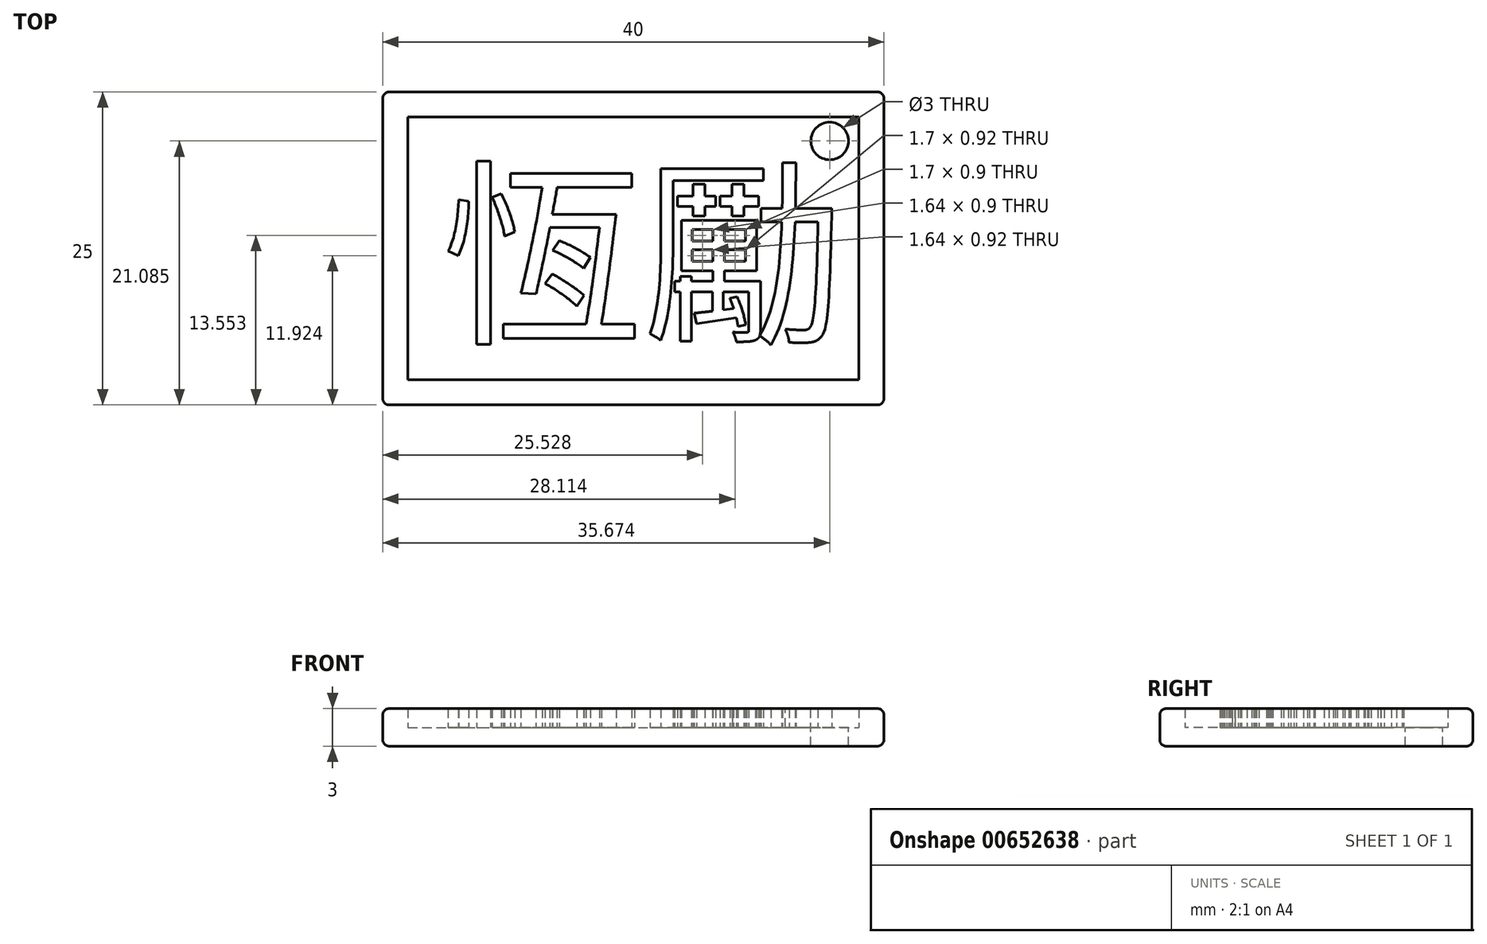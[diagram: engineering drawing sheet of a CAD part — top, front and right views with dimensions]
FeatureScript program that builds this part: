
annotation { "Feature Type Name" : "Feature", "Feature Type Description" : "" }
export const myFeature = defineFeature(function(context is Context, id is Id, definition is map)
    precondition{}
    {
        {
            var Q0;
            Q0=qCreatedBy(makeId("Top.planeOp"),FACE);
            var sketch = newSketch(context, id + "F0", { "sketchPlane" : qUnion([Q0])});
            skLineSegment(sketch, "E0.bottom", {"start": v(-20, -10.33) * mm, "end": v(20, -10.33) * mm});
            skLineSegment(sketch, "E0.top", {"start": v(20, 14.67) * mm, "end": v(-20, 14.67) * mm});
            skLineSegment(sketch, "E0.left", {"start": v(-20, -10.33) * mm, "end": v(-20, 14.67) * mm});
            skLineSegment(sketch, "E0.right", {"start": v(20, 14.67) * mm, "end": v(20, -10.33) * mm});
            skPoint(sketch, "E0.middle", {"position": v(0, 14.67) * mm});
            skSolve(sketch);
        }
        {
            var Q0;
            Q0 = qSketchRegion(id + "F0", true);
            extrude(context, id + "F1", {"entities" : qUnion([Q0]), "depth" : 1.5 * mm, "offsetDistance" : 25 * mm});
        }
        {
            var Q0;
            Q0=makeQuery(id+"F1.opExtrude","CAP_FACE",FACE,{"disambiguationData":[OSD([sQuery(id+"F0.wireOp",EDGE,"E0.bottom"),sQuery(id+"F0.wireOp",EDGE,"E0.top"),sQuery(id+"F0.wireOp",EDGE,"E0.left"),sQuery(id+"F0.wireOp",EDGE,"E0.right")])],"isStart":false});
            var sketch = newSketch(context, id + "F2", { "sketchPlane" : qUnion([Q0])});
            skLineSegment(sketch, "E1.bottom", {"start": v(-20, 14.67) * mm, "end": v(20, 14.67) * mm});
            skLineSegment(sketch, "E1.top", {"start": v(-20, -10.33) * mm, "end": v(20, -10.33) * mm});
            skLineSegment(sketch, "E1.left", {"start": v(-20, 14.67) * mm, "end": v(-20, -10.33) * mm});
            skLineSegment(sketch, "E1.right", {"start": v(20, 14.67) * mm, "end": v(20, -10.33) * mm});
            skLineSegment(sketch, "E2.0", {"start": v(-18, 12.67) * mm, "end": v(18, 12.67) * mm});
            skLineSegment(sketch, "E2.1", {"start": v(-18, 12.67) * mm, "end": v(-18, -8.33) * mm});
            skLineSegment(sketch, "E2.2", {"start": v(-18, -8.33) * mm, "end": v(18, -8.33) * mm});
            skLineSegment(sketch, "E2.3", {"start": v(18, 12.67) * mm, "end": v(18, -8.33) * mm});
            skSolve(sketch);
        }
        {
            var Q0;
            Q0 = qSketchRegion(id + "F2", true);
            extrude(context, id + "F3", {"entities" : qUnion([Q0]), "operationType" : NewBodyOperationType.ADD, "depth" : 1.5 * mm, "offsetDistance" : 25 * mm});
        }
        {
            var Q0;
            Q0=makeQuery(id+"F1.opExtrude","CAP_FACE",FACE,{"disambiguationData":[OSD([sQuery(id+"F0.wireOp",EDGE,"E0.bottom"),sQuery(id+"F0.wireOp",EDGE,"E0.top"),sQuery(id+"F0.wireOp",EDGE,"E0.left"),sQuery(id+"F0.wireOp",EDGE,"E0.right")])],"isStart":false});
            var sketch = newSketch(context, id + "F4", { "sketchPlane" : qUnion([Q0])});
            skText(sketch, "E3", { "text": "恆勵", "fontName": "NotoSansCJKtc-Regular.otf"});
            const initialGuessF4  = {"E3": [-0.01528, -0.00429, 1, 0, 0.01156]};
            skSetInitialGuess(sketch, initialGuessF4);
            skSolve(sketch);
        }
        {
            var Q0;
            Q0 = qSketchRegion(id + "F4", true);
            extrude(context, id + "F5", {"entities" : qUnion([Q0]), "depth" : 1.5 * mm, "offsetDistance" : 25 * mm});
        }
        {
            var Q0;
            Q0=makeQuery(id+"F1.opExtrude","CAP_FACE",FACE,{"disambiguationData":[OSD([sQuery(id+"F0.wireOp",EDGE,"E0.bottom"),sQuery(id+"F0.wireOp",EDGE,"E0.top"),sQuery(id+"F0.wireOp",EDGE,"E0.left"),sQuery(id+"F0.wireOp",EDGE,"E0.right")])],"isStart":false});
            var sketch = newSketch(context, id + "F6", { "sketchPlane" : qUnion([Q0])});
            skCircle(sketch, "E4", {"center": v(15.67, 10.76) * mm, "radius": 1.5 * mm});
            skSolve(sketch);
        }
        {
            var Q0;
            Q0 = qSketchRegion(id + "F6", true);
            extrude(context, id + "F7", {"entities" : qUnion([Q0]), "operationType" : NewBodyOperationType.REMOVE, "oppositeDirection" : true, "depth" : 25 * mm, "offsetDistance" : 25 * mm});
        }
        {
            var Q0;
            Q0=makeQuery(id+"F3.boolean.opBoolean","MERGE",FACE,{"derivedFrom":[makeQuery(id+"F1.opExtrude","SWEPT_FACE",FACE,{"disambiguationData":[OSD([sQuery(id+"F0.wireOp",EDGE,"E0.bottom")])]}),makeQuery(id+"F3.opExtrude","SWEPT_FACE",FACE,{"disambiguationData":[OSD([sQuery(id+"F2.wireOp",EDGE,"E1.top")])]})]});
            var Q1;
            Q1=makeQuery(id+"F3.boolean.opBoolean","MERGE",FACE,{"derivedFrom":[makeQuery(id+"F1.opExtrude","SWEPT_FACE",FACE,{"disambiguationData":[OSD([sQuery(id+"F0.wireOp",EDGE,"E0.right")])]}),makeQuery(id+"F3.opExtrude","SWEPT_FACE",FACE,{"disambiguationData":[OSD([sQuery(id+"F2.wireOp",EDGE,"E1.right")])]})]});
            var Q2;
            Q2=makeQuery(id+"F3.boolean.opBoolean","MERGE",FACE,{"derivedFrom":[makeQuery(id+"F1.opExtrude","SWEPT_FACE",FACE,{"disambiguationData":[OSD([sQuery(id+"F0.wireOp",EDGE,"E0.left")])]}),makeQuery(id+"F3.opExtrude","SWEPT_FACE",FACE,{"disambiguationData":[OSD([sQuery(id+"F2.wireOp",EDGE,"E1.left")])]})]});
            var Q3;
            Q3=makeQuery(id+"F3.boolean.opBoolean","MERGE",FACE,{"derivedFrom":[makeQuery(id+"F1.opExtrude","SWEPT_FACE",FACE,{"disambiguationData":[OSD([sQuery(id+"F0.wireOp",EDGE,"E0.top")])]}),makeQuery(id+"F3.opExtrude","SWEPT_FACE",FACE,{"disambiguationData":[OSD([sQuery(id+"F2.wireOp",EDGE,"E1.bottom")])]})]});
            fillet(context, id + "F8", {"entities" : qUnion([Q0, Q1, Q2, Q3]), "radius" : 0.5 * mm, "tangentPropagation" : true, "allowEdgeOverflow" : false});
        }
    });
